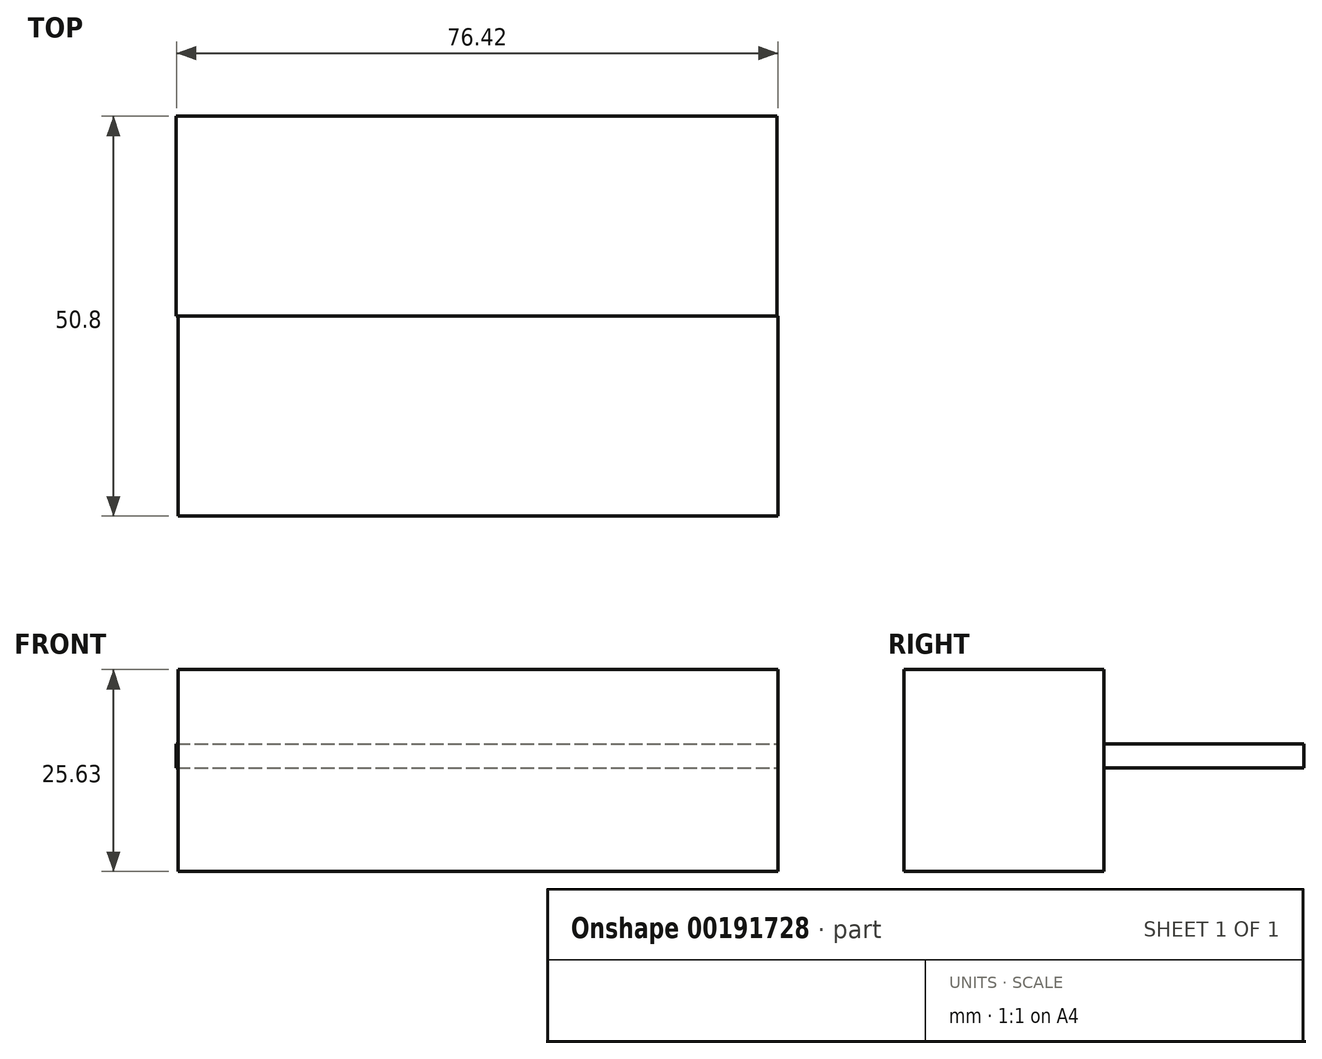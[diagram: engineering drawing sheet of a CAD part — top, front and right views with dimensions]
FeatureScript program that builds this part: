
annotation { "Feature Type Name" : "Feature", "Feature Type Description" : "" }
export const myFeature = defineFeature(function(context is Context, id is Id, definition is map)
    precondition{}
    {
        {
            var Q0;
            Q0=qCreatedBy(makeId("Front.planeOp"),FACE);
            var sketch = newSketch(context, id + "F0", { "sketchPlane" : qUnion([Q0])});
            skLineSegment(sketch, "E0.bottom", {"start": v(-31.2, 12.48) * mm, "end": v(45, 12.48) * mm});
            skLineSegment(sketch, "E0.top", {"start": v(-31.2, -13.15) * mm, "end": v(45, -13.15) * mm});
            skLineSegment(sketch, "E0.left", {"start": v(-31.2, 12.48) * mm, "end": v(-31.2, -13.15) * mm});
            skLineSegment(sketch, "E0.right", {"start": v(45, 12.48) * mm, "end": v(45, -13.15) * mm});
            skSolve(sketch);
        }
        {
            var Q0;
            Q0 = qSketchRegion(id + "F0", true);
            extrude(context, id + "F1", {"entities" : qUnion([Q0]), "depth" : 25.4 * mm});
        }
        {
            var Q0;
            Q0=qCreatedBy(makeId("Top.planeOp"),FACE);
            var sketch = newSketch(context, id + "F2", { "sketchPlane" : qUnion([Q0])});
            skLineSegment(sketch, "E1.bottom", {"start": v(-31.43, 25.4) * mm, "end": v(44.88, 25.4) * mm});
            skLineSegment(sketch, "E1.top", {"start": v(-31.43, 0) * mm, "end": v(44.88, 0) * mm});
            skLineSegment(sketch, "E1.left", {"start": v(-31.43, 25.4) * mm, "end": v(-31.43, 0) * mm});
            skLineSegment(sketch, "E1.right", {"start": v(44.88, 25.4) * mm, "end": v(44.88, 0) * mm});
            skSolve(sketch);
        }
        {
            var Q0;
            Q0 = qSketchRegion(id + "F2", true);
            extrude(context, id + "F3", {"entities" : qUnion([Q0]), "operationType" : NewBodyOperationType.ADD, "depth" : 3.05 * mm});
        }
    });
